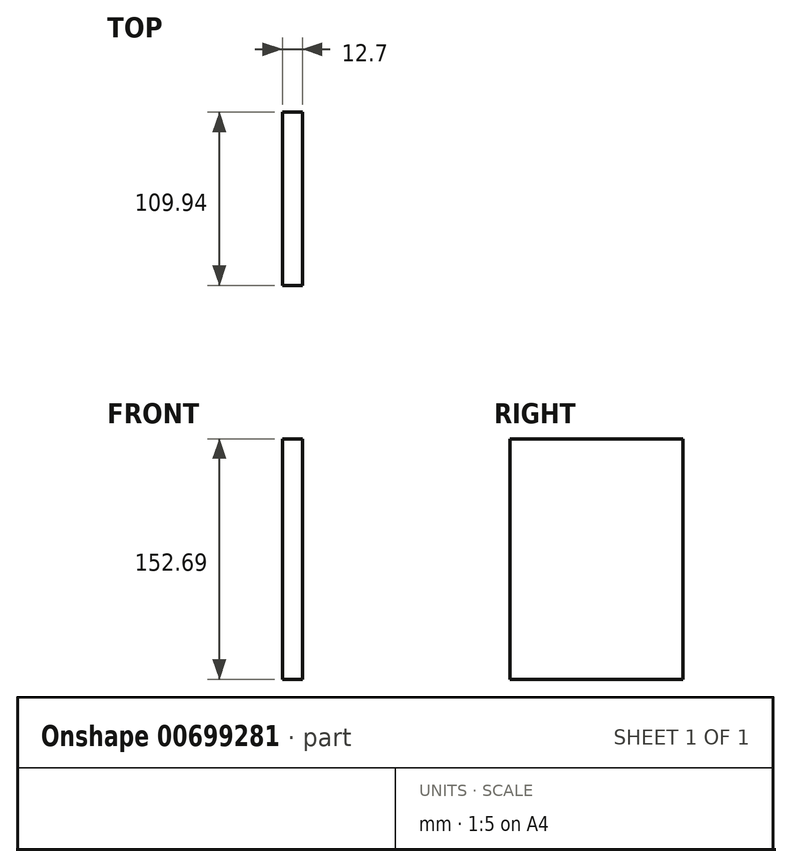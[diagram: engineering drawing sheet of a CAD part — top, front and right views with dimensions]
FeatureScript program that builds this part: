
annotation { "Feature Type Name" : "Feature", "Feature Type Description" : "" }
export const myFeature = defineFeature(function(context is Context, id is Id, definition is map)
    precondition{}
    {
        {
            var Q0;
            Q0=qCreatedBy(makeId("Right.planeOp"),FACE);
            var sketch = newSketch(context, id + "F0", { "sketchPlane" : qUnion([Q0])});
            skLineSegment(sketch, "E0.bottom", {"start": v(-51.76, 76.5) * mm, "end": v(58.18, 76.5) * mm});
            skLineSegment(sketch, "E0.top", {"start": v(-51.76, -76.2) * mm, "end": v(58.18, -76.2) * mm});
            skLineSegment(sketch, "E0.left", {"start": v(-51.76, 76.5) * mm, "end": v(-51.76, -76.2) * mm});
            skLineSegment(sketch, "E0.right", {"start": v(58.18, 76.5) * mm, "end": v(58.18, -76.2) * mm});
            skSolve(sketch);
        }
        {
            var Q0;
            Q0=makeQuery(id+"F0.imprint","IMPRINT",FACE,{"disambiguationData":[TD([[makeQuery(id+"F0.imprint","IMPRINT",EDGE,{"derivedFrom":sQuery(id+"F0.wireOp",EDGE,"E0.bottom")}),-1.0]])]});
            extrude(context, id + "F1", {"entities" : qUnion([Q0]), "depth" : 12.7 * mm, "offsetDistance" : 25.4 * mm});
        }
    });
